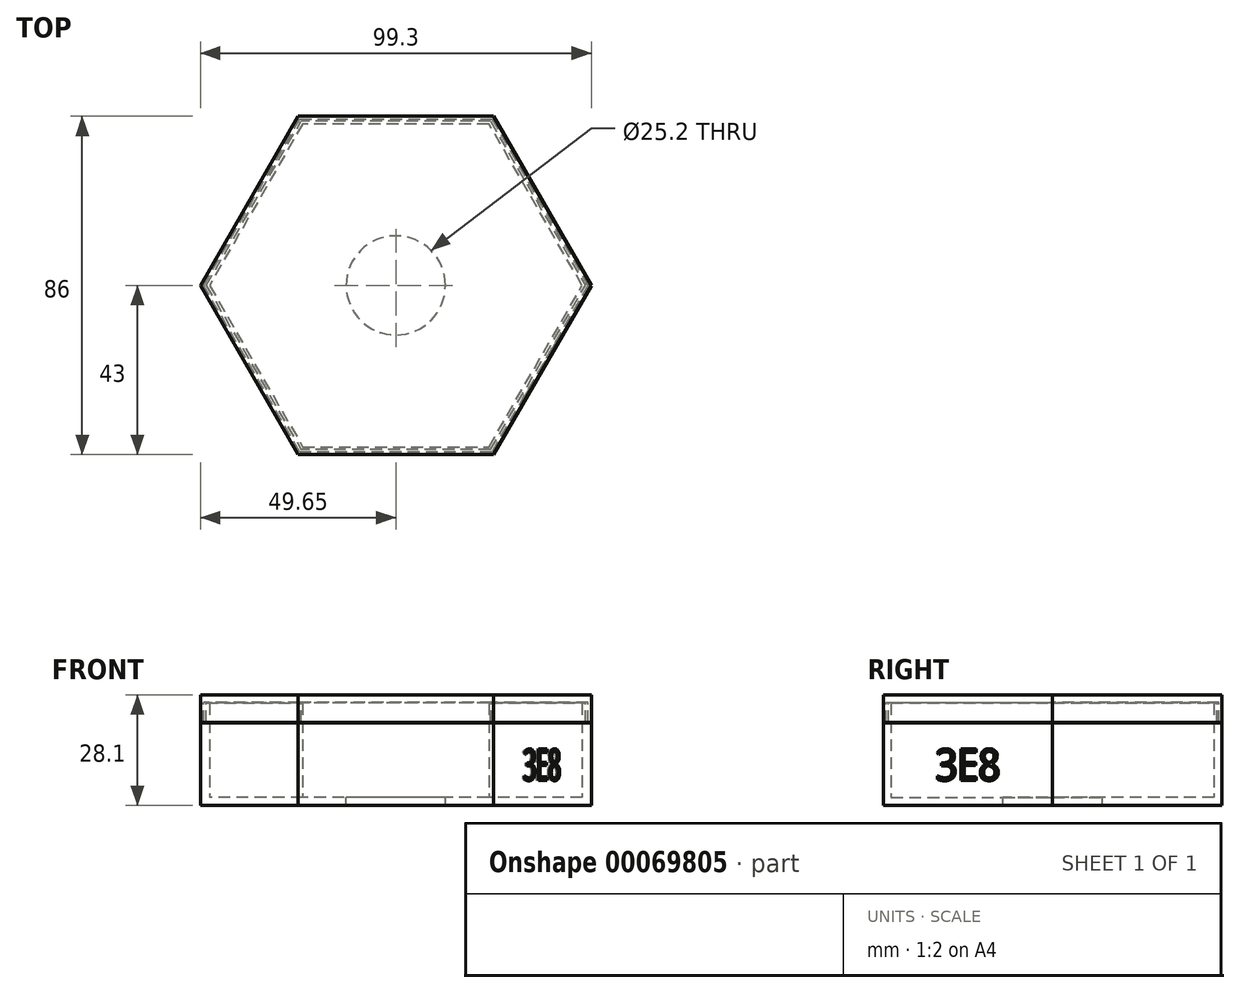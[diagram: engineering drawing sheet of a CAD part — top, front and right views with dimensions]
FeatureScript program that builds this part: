
annotation { "Feature Type Name" : "Feature", "Feature Type Description" : "" }
export const myFeature = defineFeature(function(context is Context, id is Id, definition is map)
    precondition{}
    {
        {
            var Q0;
            Q0=qCreatedBy(makeId("Top.planeOp"),FACE);
            var sketch = newSketch(context, id + "F0", { "sketchPlane" : qUnion([Q0])});
            skLineSegment(sketch, "E0.rect.bottom", {"start": v(24.83, -43) * mm, "end": v(-24.83, -43) * mm});
            skLineSegment(sketch, "E0.rect.top", {"start": v(24.83, 43) * mm, "end": v(-24.83, 43) * mm});
            skLineSegment(sketch, "E0.rect.left", {"start": v(24.83, -43) * mm, "end": v(24.83, 43) * mm, "construction": true});
            skLineSegment(sketch, "E0.rect.right", {"start": v(-24.83, -43) * mm, "end": v(-24.83, 43) * mm, "construction": true});
            skPoint(sketch, "E0.rect.middle", {"position": v(0, 0) * mm});
            skLineSegment(sketch, "E1", {"start": v(-49.65, 0) * mm, "end": v(-24.83, 43) * mm});
            skLineSegment(sketch, "E2", {"start": v(24.83, -43) * mm, "end": v(49.65, 0) * mm});
            skLineSegment(sketch, "E3", {"start": v(24.83, 43) * mm, "end": v(49.65, 0) * mm});
            skLineSegment(sketch, "E4", {"start": v(-49.65, 0) * mm, "end": v(-24.83, -43) * mm});
            skLineSegment(sketch, "E5", {"start": v(-37.24, -21.5) * mm, "end": v(37.24, 21.5) * mm, "construction": true});
            skSolve(sketch);
        }
        {
            var Q0;
            Q0 = qSketchRegion(id + "F0", true);
            extrude(context, id + "F1", {"entities" : qUnion([Q0]), "depth" : 2 * mm});
        }
        {
            var Q0;
            Q0=makeQuery(id+"F1.opExtrude","CAP_FACE",FACE,{"disambiguationData":[OSD([sQuery(id+"F0.wireOp",EDGE,"E0.rect.bottom"),sQuery(id+"F0.wireOp",EDGE,"E0.rect.top"),sQuery(id+"F0.wireOp",EDGE,"E1"),sQuery(id+"F0.wireOp",EDGE,"E2"),sQuery(id+"F0.wireOp",EDGE,"E3"),sQuery(id+"F0.wireOp",EDGE,"E4")])],"isStart":false});
            var sketch = newSketch(context, id + "F2", { "sketchPlane" : qUnion([Q0])});
            skLineSegment(sketch, "E6.0.0", {"start": v(-24.83, -43) * mm, "end": v(24.83, -43) * mm});
            skLineSegment(sketch, "E6.0.1", {"start": v(24.83, -43) * mm, "end": v(49.65, 0) * mm});
            skLineSegment(sketch, "E6.0.2", {"start": v(49.65, 0) * mm, "end": v(24.83, 43) * mm});
            skLineSegment(sketch, "E6.0.3", {"start": v(24.83, 43) * mm, "end": v(-24.83, 43) * mm});
            skLineSegment(sketch, "E6.0.4", {"start": v(-24.83, 43) * mm, "end": v(-49.65, 0) * mm});
            skLineSegment(sketch, "E6.0.5", {"start": v(-49.65, 0) * mm, "end": v(-24.83, -43) * mm});
            skLineSegment(sketch, "E7.0", {"start": v(23.67, 41) * mm, "end": v(-23.67, 41) * mm});
            skLineSegment(sketch, "E7.1", {"start": v(-47.34, 0) * mm, "end": v(-23.67, -41) * mm});
            skLineSegment(sketch, "E7.2", {"start": v(-23.67, -41) * mm, "end": v(23.67, -41) * mm});
            skLineSegment(sketch, "E7.3", {"start": v(-23.67, 41) * mm, "end": v(-47.34, 0) * mm});
            skLineSegment(sketch, "E7.4", {"start": v(23.67, -41) * mm, "end": v(47.34, 0) * mm});
            skLineSegment(sketch, "E7.5", {"start": v(47.34, 0) * mm, "end": v(23.67, 41) * mm});
            skSolve(sketch);
        }
        {
            var Q0;
            Q0 = qSketchRegion(id + "F2", true);
            extrude(context, id + "F3", {"entities" : qUnion([Q0]), "operationType" : NewBodyOperationType.ADD, "depth" : 24 * mm});
        }
        {
            var Q0;
            Q0=makeQuery(id+"F3.opExtrude","CAP_FACE",FACE,{"disambiguationData":[OSD([sQuery(id+"F2.wireOp",EDGE,"E6.0.0"),sQuery(id+"F2.wireOp",EDGE,"E6.0.1"),sQuery(id+"F2.wireOp",EDGE,"E6.0.2"),sQuery(id+"F2.wireOp",EDGE,"E6.0.3"),sQuery(id+"F2.wireOp",EDGE,"E6.0.4"),sQuery(id+"F2.wireOp",EDGE,"E6.0.5"),sQuery(id+"F2.wireOp",EDGE,"E7.0"),sQuery(id+"F2.wireOp",EDGE,"E7.1"),sQuery(id+"F2.wireOp",EDGE,"E7.2"),sQuery(id+"F2.wireOp",EDGE,"E7.3"),sQuery(id+"F2.wireOp",EDGE,"E7.4"),sQuery(id+"F2.wireOp",EDGE,"E7.5")])],"isStart":false});
            var sketch = newSketch(context, id + "F4", { "sketchPlane" : qUnion([Q0])});
            skLineSegment(sketch, "E8.0", {"start": v(-49.65, 0) * mm, "end": v(-24.83, 43) * mm});
            skLineSegment(sketch, "E9.0", {"start": v(24.83, 43) * mm, "end": v(-24.83, 43) * mm});
            skLineSegment(sketch, "E10.0", {"start": v(24.83, 43) * mm, "end": v(49.65, 0) * mm});
            skLineSegment(sketch, "E11.0", {"start": v(24.83, -43) * mm, "end": v(49.65, 0) * mm});
            skLineSegment(sketch, "E12.0", {"start": v(24.83, -43) * mm, "end": v(-24.83, -43) * mm});
            skLineSegment(sketch, "E13.0", {"start": v(-49.65, 0) * mm, "end": v(-24.83, -43) * mm});
            skLineSegment(sketch, "E14.0", {"start": v(-48.15, 0) * mm, "end": v(-24.08, -41.7) * mm});
            skLineSegment(sketch, "E14.1", {"start": v(24.08, 41.7) * mm, "end": v(-24.08, 41.7) * mm});
            skLineSegment(sketch, "E14.2", {"start": v(24.08, 41.7) * mm, "end": v(48.15, 0) * mm});
            skLineSegment(sketch, "E14.3", {"start": v(-48.15, 0) * mm, "end": v(-24.08, 41.7) * mm});
            skLineSegment(sketch, "E14.4", {"start": v(24.08, -41.7) * mm, "end": v(48.15, 0) * mm});
            skLineSegment(sketch, "E14.5", {"start": v(24.08, -41.7) * mm, "end": v(-24.08, -41.7) * mm});
            skSolve(sketch);
        }
        {
            var Q0;
            Q0 = qSketchRegion(id + "F4", true);
            extrude(context, id + "F5", {"entities" : qUnion([Q0]), "operationType" : NewBodyOperationType.REMOVE, "oppositeDirection" : true, "depth" : 5 * mm});
        }
        {
            var Q0;
            Q0=makeQuery(id+"F3.boolean.opBoolean","MERGE",FACE,{"derivedFrom":[makeQuery(id+"F1.opExtrude","SWEPT_FACE",FACE,{"disambiguationData":[OSD([sQuery(id+"F0.wireOp",EDGE,"E2")])]}),makeQuery(id+"F3.opExtrude","SWEPT_FACE",FACE,{"disambiguationData":[OSD([sQuery(id+"F2.wireOp",EDGE,"E6.0.1")])]})]});
            var sketch = newSketch(context, id + "F6", { "sketchPlane" : qUnion([Q0])});
            skText(sketch, "E15", { "text": "3E8", "fontName": "OpenSans-Regular.ttf"});
            skLineSegment(sketch, "E16", {"start": v(24.83, 21) * mm, "end": v(-24.83, 0) * mm, "construction": true});
            skPoint(sketch, "E17", {"position": v(-0.34, 10.36) * mm});
            skPoint(sketch, "E17.positionSnap0", {"position": v(8.83, 10.36) * mm});
            const initialGuessF6  = {"E15": [-0.0095, 0.00635, 1, 0, 0.008]};
            skSetInitialGuess(sketch, initialGuessF6);
            skSolve(sketch);
        }
        {
            var Q0;
            Q0 = qSketchRegion(id + "F6", true);
            extrude(context, id + "F7", {"entities" : qUnion([Q0]), "operationType" : NewBodyOperationType.REMOVE, "oppositeDirection" : true, "depth" : .5 * mm});
        }
        {
            var Q0;
            Q0=makeQuery(id+"F1.opExtrude","CAP_FACE",FACE,{"disambiguationData":[OSD([sQuery(id+"F0.wireOp",EDGE,"E0.rect.bottom"),sQuery(id+"F0.wireOp",EDGE,"E0.rect.top"),sQuery(id+"F0.wireOp",EDGE,"E1"),sQuery(id+"F0.wireOp",EDGE,"E2"),sQuery(id+"F0.wireOp",EDGE,"E3"),sQuery(id+"F0.wireOp",EDGE,"E4")])],"isStart":false});
            var sketch = newSketch(context, id + "F8", { "sketchPlane" : qUnion([Q0])});
            skCircle(sketch, "E18", {"center": v(0, 0) * mm, "radius": 12.6 * mm});
            skSolve(sketch);
        }
        {
            var Q0;
            Q0 = qSketchRegion(id + "F8", true);
            extrude(context, id + "F9", {"entities" : qUnion([Q0]), "operationType" : NewBodyOperationType.REMOVE, "endBound" : BoundingType.THROUGH_ALL, "oppositeDirection" : true, "depth" : 25 * mm});
        }
        {
            var Q0;
            Q0=makeQuery(id+"F3.opExtrude","CAP_FACE",FACE,{"disambiguationData":[OSD([sQuery(id+"F2.wireOp",EDGE,"E6.0.0"),sQuery(id+"F2.wireOp",EDGE,"E6.0.1"),sQuery(id+"F2.wireOp",EDGE,"E6.0.2"),sQuery(id+"F2.wireOp",EDGE,"E6.0.3"),sQuery(id+"F2.wireOp",EDGE,"E6.0.4"),sQuery(id+"F2.wireOp",EDGE,"E6.0.5"),sQuery(id+"F2.wireOp",EDGE,"E7.0"),sQuery(id+"F2.wireOp",EDGE,"E7.1"),sQuery(id+"F2.wireOp",EDGE,"E7.2"),sQuery(id+"F2.wireOp",EDGE,"E7.3"),sQuery(id+"F2.wireOp",EDGE,"E7.4"),sQuery(id+"F2.wireOp",EDGE,"E7.5")])],"isStart":false});
            cPlane(context, id + "F10", {"entities" : qUnion([Q0]), "cplaneType" : CPlaneType.OFFSET, "offset" : .1 * mm, "width" : 150 * mm, "height" : 150 * mm});
        }
        {
            var Q0;
            Q0=qCreatedBy(id+"F10.planeOp",FACE);
            var sketch = newSketch(context, id + "F11", { "sketchPlane" : qUnion([Q0])});
            skLineSegment(sketch, "E19.0", {"start": v(24.83, -43) * mm, "end": v(-24.83, -43) * mm});
            skLineSegment(sketch, "E20.0", {"start": v(24.83, -43) * mm, "end": v(49.65, 0) * mm});
            skLineSegment(sketch, "E21.0", {"start": v(24.83, 43) * mm, "end": v(49.65, 0) * mm});
            skLineSegment(sketch, "E22.0", {"start": v(-49.65, 0) * mm, "end": v(-24.83, -43) * mm});
            skLineSegment(sketch, "E23.0", {"start": v(-49.65, 0) * mm, "end": v(-24.83, 43) * mm});
            skLineSegment(sketch, "E24.0", {"start": v(24.83, 43) * mm, "end": v(-24.83, 43) * mm});
            skSolve(sketch);
        }
        {
            var Q0;
            Q0 = qSketchRegion(id + "F11", true);
            extrude(context, id + "F12", {"entities" : qUnion([Q0]), "depth" : 2 * mm});
        }
        {
            var Q0;
            Q0=makeQuery(id+"F12.opExtrude","CAP_FACE",FACE,{"disambiguationData":[OSD([sQuery(id+"F11.wireOp",EDGE,"E19.0"),sQuery(id+"F11.wireOp",EDGE,"E20.0"),sQuery(id+"F11.wireOp",EDGE,"E21.0"),sQuery(id+"F11.wireOp",EDGE,"E22.0"),sQuery(id+"F11.wireOp",EDGE,"E23.0"),sQuery(id+"F11.wireOp",EDGE,"E24.0")])],"isStart":true});
            var sketch = newSketch(context, id + "F13", { "sketchPlane" : qUnion([Q0])});
            skLineSegment(sketch, "E25.0.0", {"start": v(24.83, 43) * mm, "end": v(-24.83, 43) * mm});
            skLineSegment(sketch, "E25.0.1", {"start": v(-24.83, 43) * mm, "end": v(-49.65, 0) * mm});
            skLineSegment(sketch, "E25.0.2", {"start": v(-49.65, 0) * mm, "end": v(-24.83, -43) * mm});
            skLineSegment(sketch, "E25.0.3", {"start": v(-24.83, -43) * mm, "end": v(24.83, -43) * mm});
            skLineSegment(sketch, "E25.0.4", {"start": v(24.83, -43) * mm, "end": v(49.65, 0) * mm});
            skLineSegment(sketch, "E25.0.5", {"start": v(49.65, 0) * mm, "end": v(24.83, 43) * mm});
            skLineSegment(sketch, "E26.0", {"start": v(24.42, 42.3) * mm, "end": v(-24.42, 42.3) * mm});
            skLineSegment(sketch, "E26.1", {"start": v(-48.84, 0) * mm, "end": v(-24.42, -42.3) * mm});
            skLineSegment(sketch, "E26.2", {"start": v(-24.42, -42.3) * mm, "end": v(24.42, -42.3) * mm});
            skLineSegment(sketch, "E26.3", {"start": v(-24.42, 42.3) * mm, "end": v(-48.84, 0) * mm});
            skLineSegment(sketch, "E26.4", {"start": v(24.42, -42.3) * mm, "end": v(48.84, 0) * mm});
            skLineSegment(sketch, "E26.5", {"start": v(48.84, 0) * mm, "end": v(24.42, 42.3) * mm});
            skSolve(sketch);
        }
        {
            var Q0;
            Q0 = qSketchRegion(id + "F13", true);
            extrude(context, id + "F14", {"entities" : qUnion([Q0]), "operationType" : NewBodyOperationType.ADD, "depth" : 5 * mm});
        }
    });
